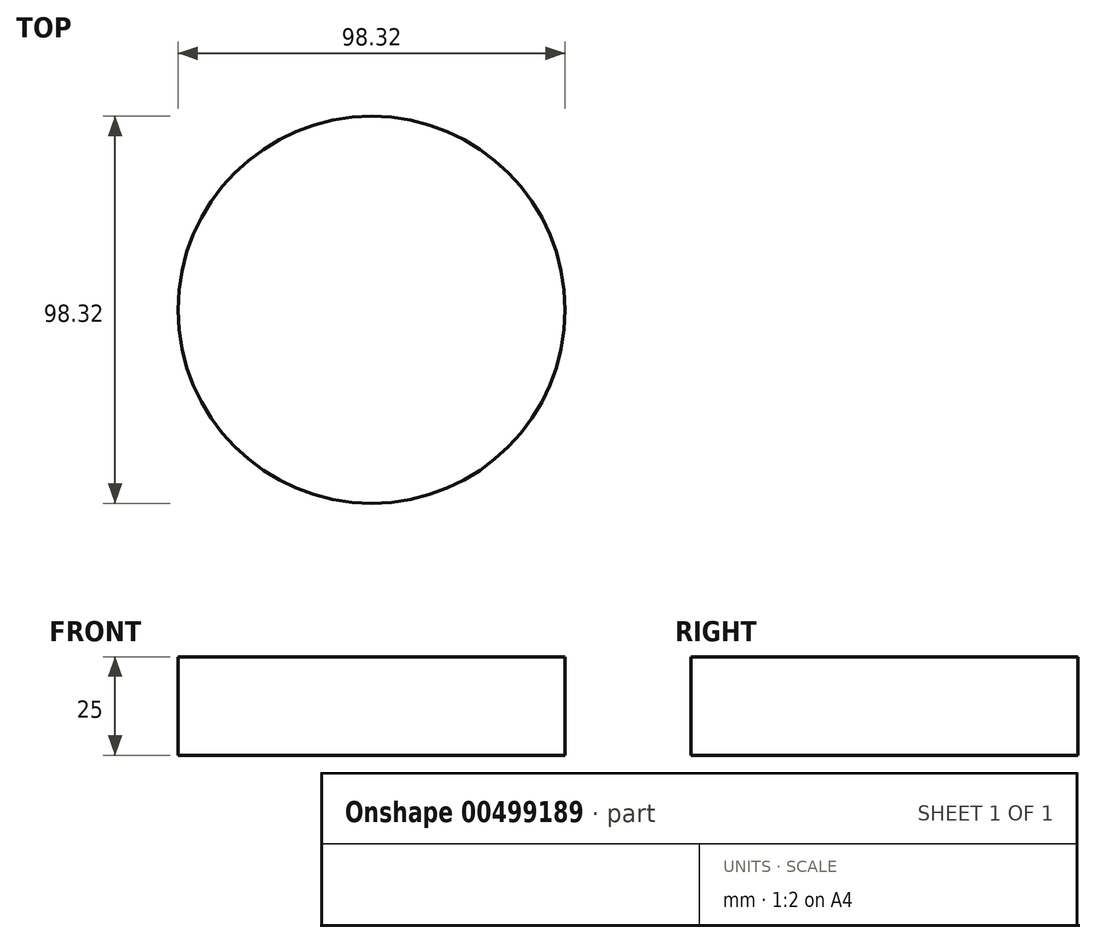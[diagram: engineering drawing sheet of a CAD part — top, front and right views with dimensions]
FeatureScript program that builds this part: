
annotation { "Feature Type Name" : "Feature", "Feature Type Description" : "" }
export const myFeature = defineFeature(function(context is Context, id is Id, definition is map)
    precondition{}
    {
        {
            var Q0;
            Q0=qCreatedBy(makeId("Top.planeOp"),FACE);
            var sketch = newSketch(context, id + "F0", { "sketchPlane" : qUnion([Q0])});
            skCircle(sketch, "E0", {"center": v(0, 0) * mm, "radius": 49.16 * mm});
            skLineSegment(sketch, "E1", {"start": v(-73.71, 0) * mm, "end": v(82.5, 0) * mm, "construction": true});
            skSolve(sketch);
        }
        {
            var Q0;
            Q0=makeQuery(id+"F0.imprint","IMPRINT",FACE,{"disambiguationData":[TD([[makeQuery(id+"F0.imprint","IMPRINT",EDGE,{"derivedFrom":sQuery(id+"F0.wireOp",EDGE,"E0")}),1.0]])]});
            extrude(context, id + "F1", {"entities" : qUnion([Q0]), "depth" : 25 * mm});
        }
    });
